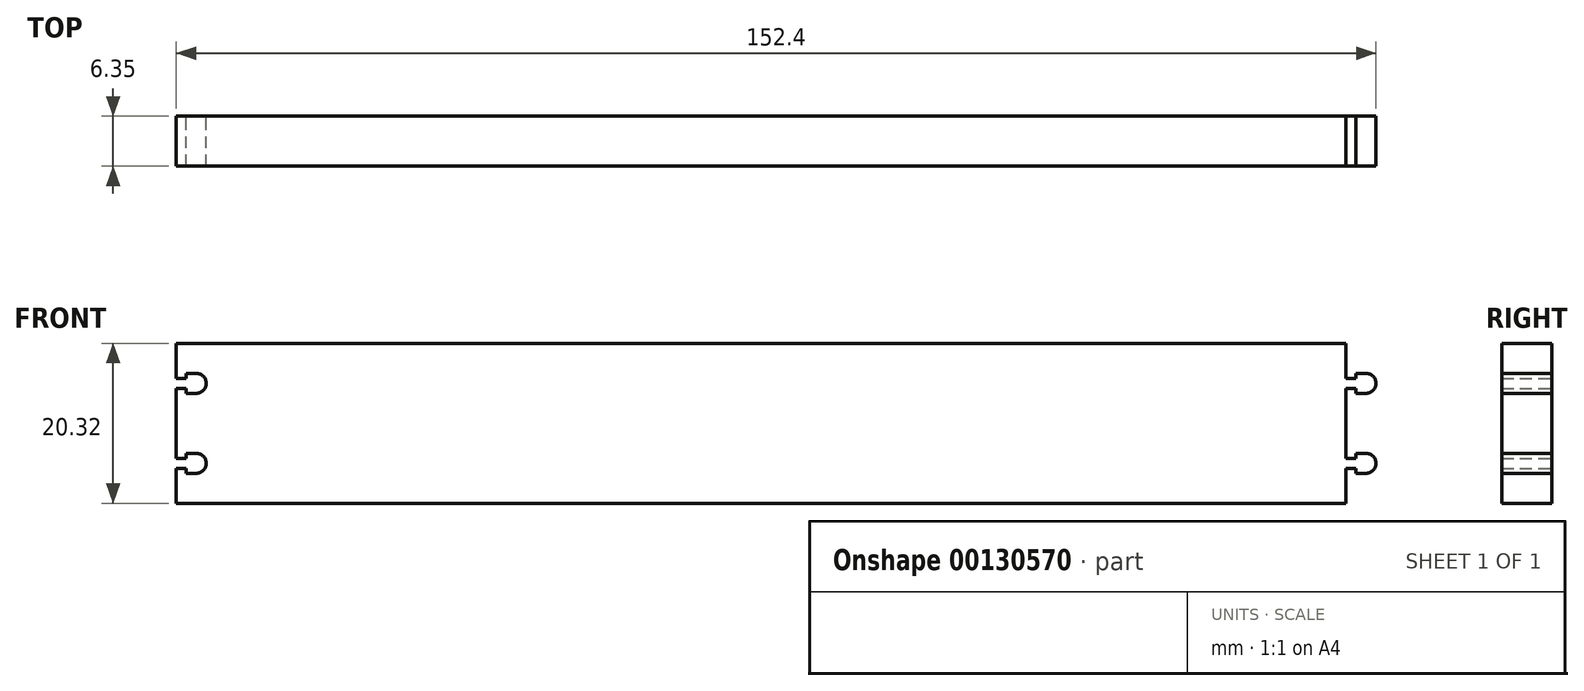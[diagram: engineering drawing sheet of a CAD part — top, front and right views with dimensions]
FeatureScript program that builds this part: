
annotation { "Feature Type Name" : "Feature", "Feature Type Description" : "" }
export const myFeature = defineFeature(function(context is Context, id is Id, definition is map)
    precondition{}
    {
        {
            var Q0;
            Q0=qCreatedBy(makeId("Front.planeOp"),FACE);
            var sketch = newSketch(context, id + "F0", { "sketchPlane" : qUnion([Q0])});
            skLineSegment(sketch, "E0.bottom", {"start": v(72.39, -10.16) * mm, "end": v(-76.2, -10.16) * mm});
            skLineSegment(sketch, "E0.top", {"start": v(72.39, 10.16) * mm, "end": v(-76.2, 10.16) * mm});
            skLineSegment(sketch, "E0.right", {"start": v(-76.2, -10.16) * mm, "end": v(-76.2, -5.72) * mm});
            skPoint(sketch, "E0.middle", {"position": v(0, 0) * mm});
            skLineSegment(sketch, "E1", {"start": v(-74.93, 6.35) * mm, "end": v(-73.66, 6.35) * mm});
            skArc(sketch, "E2", {"start": v(-73.66, 3.81) * mm, "mid": v(-72.39, 5.08) * mm, "end": v(-73.66, 6.35) * mm});
            skLineSegment(sketch, "E3", {"start": v(-74.93, 6.35) * mm, "end": v(-74.93, 5.72) * mm});
            skLineSegment(sketch, "E4", {"start": v(-74.93, 5.72) * mm, "end": v(-76.2, 5.72) * mm});
            skLineSegment(sketch, "E5", {"start": v(-74.93, 4.45) * mm, "end": v(-74.93, 3.81) * mm});
            skLineSegment(sketch, "E6", {"start": v(-74.93, 4.45) * mm, "end": v(-76.2, 4.45) * mm});
            skLineSegment(sketch, "E7.trimOffspring", {"start": v(-76.2, 5.72) * mm, "end": v(-76.2, 10.16) * mm});
            skLineSegment(sketch, "E8", {"start": v(-74.93, 3.81) * mm, "end": v(-73.66, 3.81) * mm});
            skLineSegment(sketch, "E9.MirrorCS", {"start": v(-74.93, -4.45) * mm, "end": v(-76.2, -4.45) * mm});
            skLineSegment(sketch, "E10.MirrorCS", {"start": v(-74.93, -5.72) * mm, "end": v(-76.2, -5.72) * mm});
            skLineSegment(sketch, "E11.MirrorCS", {"start": v(-74.93, -6.35) * mm, "end": v(-74.93, -5.72) * mm});
            skLineSegment(sketch, "E12.MirrorCS", {"start": v(-74.93, -6.35) * mm, "end": v(-73.66, -6.35) * mm});
            skArc(sketch, "E13.MirrorCS", {"start": v(-73.66, -3.81) * mm, "mid": v(-72.39, -5.08) * mm, "end": v(-73.66, -6.35) * mm});
            skLineSegment(sketch, "E14.MirrorCS", {"start": v(-74.93, -3.81) * mm, "end": v(-73.66, -3.81) * mm});
            skLineSegment(sketch, "E15.MirrorCS", {"start": v(-74.93, -4.45) * mm, "end": v(-74.93, -3.81) * mm});
            skLineSegment(sketch, "E16.trimOffspring", {"start": v(-76.2, -4.45) * mm, "end": v(-76.2, 4.45) * mm});
            skLineSegment(sketch, "E17.MirrorCS", {"start": v(74.93, 6.35) * mm, "end": v(73.66, 6.35) * mm});
            skLineSegment(sketch, "E18.MirrorCS", {"start": v(74.93, 3.81) * mm, "end": v(73.66, 3.81) * mm});
            skArc(sketch, "E19.MirrorCS", {"start": v(74.93, 3.81) * mm, "mid": v(76.2, 5.08) * mm, "end": v(74.93, 6.35) * mm});
            skLineSegment(sketch, "E20.MirrorCS", {"start": v(73.66, 5.72) * mm, "end": v(72.39, 5.72) * mm});
            skLineSegment(sketch, "E21.MirrorCS", {"start": v(73.66, 6.35) * mm, "end": v(73.66, 5.72) * mm});
            skLineSegment(sketch, "E22.MirrorCS", {"start": v(73.66, 4.45) * mm, "end": v(72.39, 4.45) * mm});
            skLineSegment(sketch, "E23.MirrorCS", {"start": v(73.66, 4.45) * mm, "end": v(73.66, 3.81) * mm});
            skLineSegment(sketch, "E24", {"start": v(72.39, 10.16) * mm, "end": v(72.39, 5.72) * mm});
            skLineSegment(sketch, "E25.trimOffspring", {"start": v(72.39, 4.45) * mm, "end": v(72.39, -4.45) * mm});
            skLineSegment(sketch, "E26.MirrorCS", {"start": v(73.66, -4.45) * mm, "end": v(72.39, -4.45) * mm});
            skLineSegment(sketch, "E27.MirrorCS", {"start": v(73.66, -5.72) * mm, "end": v(72.39, -5.72) * mm});
            skLineSegment(sketch, "E28.MirrorCS", {"start": v(73.66, -6.35) * mm, "end": v(73.66, -5.72) * mm});
            skArc(sketch, "E29.MirrorCS", {"start": v(74.93, -3.81) * mm, "mid": v(76.2, -5.08) * mm, "end": v(74.93, -6.35) * mm});
            skLineSegment(sketch, "E30.MirrorCS", {"start": v(74.93, -6.35) * mm, "end": v(73.66, -6.35) * mm});
            skLineSegment(sketch, "E31.MirrorCS", {"start": v(74.93, -3.81) * mm, "end": v(73.66, -3.81) * mm});
            skLineSegment(sketch, "E32.MirrorCS", {"start": v(73.66, -4.45) * mm, "end": v(73.66, -3.81) * mm});
            skLineSegment(sketch, "E33.trimOffspring", {"start": v(72.39, -5.72) * mm, "end": v(72.39, -10.16) * mm});
            skSolve(sketch);
        }
        {
            var Q0;
            Q0 = qSketchRegion(id + "F0", true);
            extrude(context, id + "F1", {"entities" : qUnion([Q0]), "depth" : 6.35 * mm});
        }
    });
